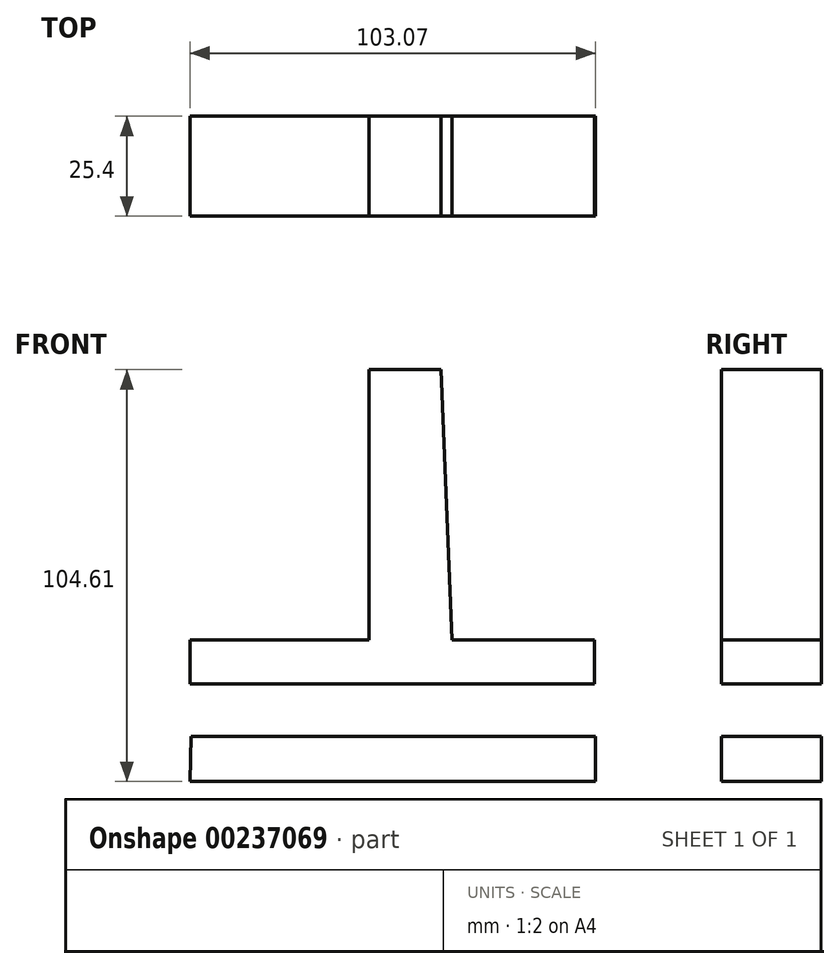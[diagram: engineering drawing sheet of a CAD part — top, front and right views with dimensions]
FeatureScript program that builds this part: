
annotation { "Feature Type Name" : "Feature", "Feature Type Description" : "" }
export const myFeature = defineFeature(function(context is Context, id is Id, definition is map)
    precondition{}
    {
        {
            var Q0;
            Q0=qCreatedBy(makeId("Front.planeOp"),FACE);
            var sketch = newSketch(context, id + "F0", { "sketchPlane" : qUnion([Q0])});
            skLineSegment(sketch, "E0", {"start": v(-55.71, -22.75) * mm, "end": v(47.05, -22.75) * mm});
            skLineSegment(sketch, "E1", {"start": v(-55.71, -22.75) * mm, "end": v(-55.71, -33.9) * mm});
            skLineSegment(sketch, "E2", {"start": v(-55.71, -33.9) * mm, "end": v(47.05, -33.9) * mm});
            skLineSegment(sketch, "E3", {"start": v(47.05, -33.9) * mm, "end": v(47.05, -22.75) * mm});
            skLineSegment(sketch, "E4", {"start": v(-10.21, -22.75) * mm, "end": v(-10.21, 45.96) * mm});
            skLineSegment(sketch, "E5", {"start": v(-10.21, 45.96) * mm, "end": v(8.05, 45.96) * mm});
            skLineSegment(sketch, "E6", {"start": v(8.05, 45.96) * mm, "end": v(10.83, -22.75) * mm});
            skLineSegment(sketch, "E7", {"start": v(-55.4, -47.2) * mm, "end": v(47.36, -47.2) * mm});
            skLineSegment(sketch, "E8", {"start": v(47.36, -47.2) * mm, "end": v(47.36, -58.65) * mm});
            skLineSegment(sketch, "E9", {"start": v(47.36, -58.65) * mm, "end": v(-55.71, -58.65) * mm});
            skLineSegment(sketch, "E10", {"start": v(-55.71, -58.65) * mm, "end": v(-55.4, -47.2) * mm});
            skSolve(sketch);
        }
        {
            var Q0;
            {var subQ0=sQuery(id+"F0.wireOp",EDGE,"E4");Q0=makeQuery(id+"F0.imprint","IMPRINT",FACE,{"disambiguationData":[TD([[makeQuery(id+"F0.imprint","IMPRINT",EDGE,{"derivedFrom":subQ0}),-1.0]])]});}
            var Q1;
            {var subQ0=sQuery(id+"F0.wireOp",EDGE,"E1");Q1=makeQuery(id+"F0.imprint","IMPRINT",FACE,{"disambiguationData":[TD([[makeQuery(id+"F0.imprint","IMPRINT",EDGE,{"derivedFrom":subQ0}),1.0]])]});}
            var Q2;
            Q2=makeQuery(id+"F0.imprint","IMPRINT",FACE,{"disambiguationData":[TD([[makeQuery(id+"F0.imprint","IMPRINT",EDGE,{"derivedFrom":sQuery(id+"F0.wireOp",EDGE,"E7")}),-1.0]])]});
            extrude(context, id + "F1", {"entities" : qUnion([Q0, Q1, Q2]), "depth" : 25.4 * mm});
        }
    });
